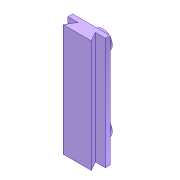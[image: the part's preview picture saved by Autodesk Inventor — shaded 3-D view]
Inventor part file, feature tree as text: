
AUTODESK INVENTOR PART (.ipt)
format: ipt  version: unknown  size: 189,952 bytes
history: native  units: mm
features: sketch x2, extrude x1, revolve x1, mirror x1
ambient origin geometry x8: Origin, YZ Plane, XZ Plane, XY Plane, X Axis, Y Axis, Z Axis, Center Point
feature tree (5):
  extrude  "Extrusion1"  Depth=2.0mm
  revolve  "Revolution1"  [1 undecoded]
  mirror  "Mirror1"
  sketch  "Sketch1"  dims[d0=6.0mm d1=2.0mm]
  sketch  "Sketch2"  dims[d2=2.0mm d3=1.0mm d4=8.0mm d5=60.0deg d6=60.0deg d7=24.0mm d8=0.0mm d9=8.0mm d10=2.0mm d11=3.0mm d12=0.5mm d13=2.0mm d14=90.0deg]
note: 1 required parameter value undecoded (feature->parameter linkage not recoverable at this tier; creation-order binding heuristic only, values carry confidence <= 0.55)
